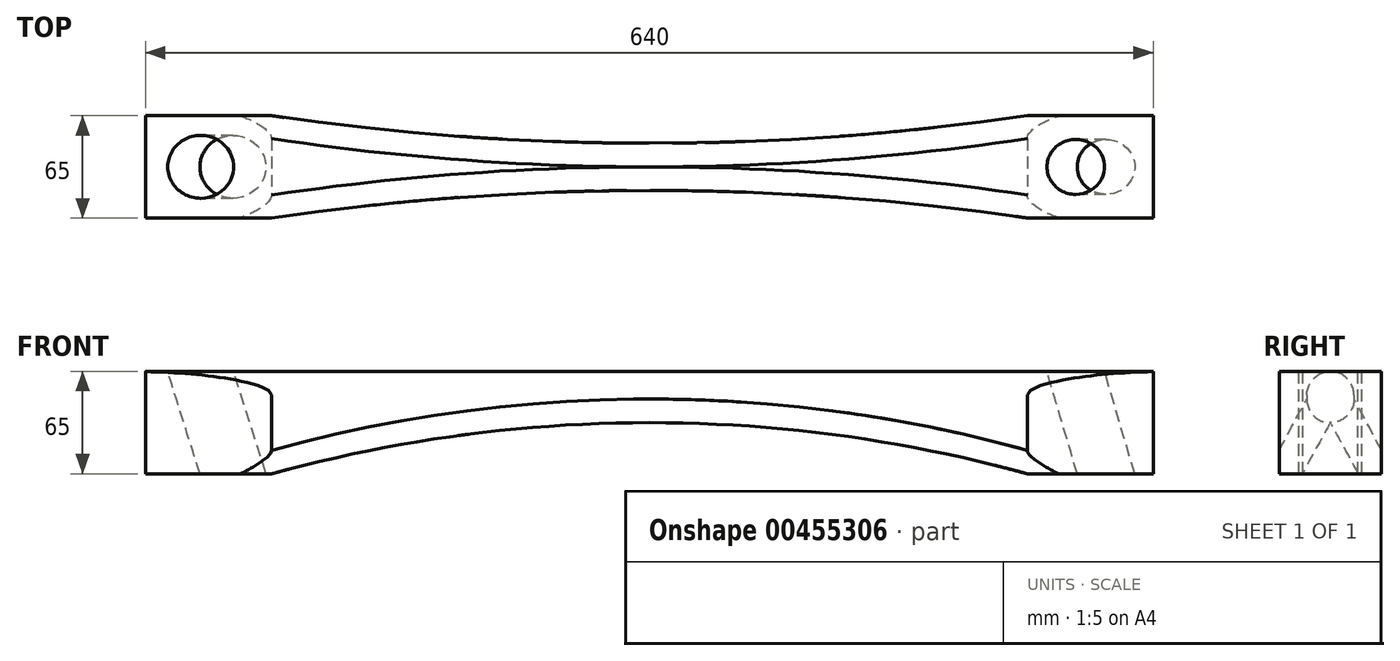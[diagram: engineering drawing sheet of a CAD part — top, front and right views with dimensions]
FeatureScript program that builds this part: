
annotation { "Feature Type Name" : "Feature", "Feature Type Description" : "" }
export const myFeature = defineFeature(function(context is Context, id is Id, definition is map)
    precondition{}
    {
        {
            var Q0;
            Q0=qCreatedBy(makeId("Front.planeOp"),FACE);
            var sketch = newSketch(context, id + "F0", { "sketchPlane" : qUnion([Q0])});
            skLineSegment(sketch, "E0.bottom", {"start": v(0, 0) * mm, "end": v(-640, 0) * mm});
            skLineSegment(sketch, "E0.top", {"start": v(0, 65) * mm, "end": v(-640, 65) * mm});
            skLineSegment(sketch, "E0.left", {"start": v(0, 0) * mm, "end": v(0, 65) * mm});
            skLineSegment(sketch, "E0.right", {"start": v(-640, 0) * mm, "end": v(-640, 65) * mm});
            skSolve(sketch);
        }
        {
            var Q0;
            Q0 = qSketchRegion(id + "F0", true);
            extrude(context, id + "F1", {"entities" : qUnion([Q0]), "depth" : 65 * mm, "offsetDistance" : 25 * mm});
        }
        {
            var Q0;
            Q0=makeQuery(id+"F1.opExtrude","SWEPT_FACE",FACE,{"disambiguationData":[OSD([sQuery(id+"F0.wireOp",EDGE,"E0.bottom")])]});
            var sketch = newSketch(context, id + "F2", { "sketchPlane" : qUnion([Q0])});
            skLineSegment(sketch, "E1", {"start": v(-30, 65) * mm, "end": v(-30, 0) * mm, "construction": true});
            skLineSegment(sketch, "E2", {"start": v(-601, 65) * mm, "end": v(-601, 0) * mm, "construction": true});
            skSolve(sketch);
        }
        {
            var Q0;
            Q0=sQuery(id+"F2.wireOp",EDGE,"E1");
            cPlane(context, id + "F3", {"entities" : qUnion([Q0]), "cplaneType" : CPlaneType.LINE_ANGLE, "offset" : 25 * mm, "angle" : 16.5 * degree, "oppositeDirection" : true, "width" : 150 * mm, "height" : 150 * mm});
        }
        {
            var Q0;
            Q0=qCreatedBy(id+"F3.planeOp",FACE);
            var sketch = newSketch(context, id + "F4", { "sketchPlane" : qUnion([Q0])});
            skLineSegment(sketch, "E3.0", {"start": v(0, -65) * mm, "end": v(0, 0) * mm, "construction": true});
            skLineSegment(sketch, "E4", {"start": v(0, -32.5) * mm, "end": v(-90.45, -32.5) * mm, "construction": true});
            skLineSegment(sketch, "E5.0", {"start": v(-28.76, -65) * mm, "end": v(-28.76, 0) * mm, "construction": true});
            skCircle(sketch, "E6", {"center": v(-28.76, -32.5) * mm, "radius": 17.5 * mm});
            skSolve(sketch);
        }
        {
            var Q0;
            Q0 = qSketchRegion(id + "F4", true);
            extrude(context, id + "F5", {"entities" : qUnion([Q0]), "operationType" : NewBodyOperationType.REMOVE, "oppositeDirection" : true, "depth" : 8 * mm, "offsetDistance" : 25 * mm, "hasSecondDirection" : true, "secondDirectionOppositeDirection" : false, "secondDirectionDepth" : 87 * mm});
        }
        {
            var Q0;
            Q0=makeQuery(id+"F1.opExtrude","SWEPT_FACE",FACE,{"disambiguationData":[OSD([sQuery(id+"F0.wireOp",EDGE,"E0.top")])]});
            var sketch = newSketch(context, id + "F6", { "sketchPlane" : qUnion([Q0])});
            skLineSegment(sketch, "E7", {"start": v(-605, 0) * mm, "end": v(-605, -65) * mm, "construction": true});
            skSolve(sketch);
        }
        {
            var Q0;
            Q0=sQuery(id+"F6.wireOp",EDGE,"E7");
            cPlane(context, id + "F7", {"entities" : qUnion([Q0]), "cplaneType" : CPlaneType.LINE_ANGLE, "offset" : 25 * mm, "angle" : 17.5 * degree, "width" : 150 * mm, "height" : 150 * mm});
        }
        {
            var Q0;
            Q0=qCreatedBy(id+"F7.planeOp",FACE);
            var sketch = newSketch(context, id + "F8", { "sketchPlane" : qUnion([Q0])});
            skLineSegment(sketch, "E8.0", {"start": v(-590.83, 65) * mm, "end": v(-590.83, 0) * mm, "construction": true});
            skLineSegment(sketch, "E9", {"start": v(-590.83, 32.5) * mm, "end": v(-455.25, 32.5) * mm, "construction": true});
            skLineSegment(sketch, "E10.0", {"start": v(-557.45, 0) * mm, "end": v(-557.45, 65) * mm, "construction": true});
            skCircle(sketch, "E11", {"center": v(-557.45, 32.5) * mm, "radius": 20 * mm});
            skSolve(sketch);
        }
        {
            var Q0;
            Q0 = qSketchRegion(id + "F8", true);
            extrude(context, id + "F9", {"entities" : qUnion([Q0]), "operationType" : NewBodyOperationType.REMOVE, "depth" : 92 * mm, "offsetDistance" : 25 * mm, "hasSecondDirection" : true, "secondDirectionOppositeDirection" : true, "secondDirectionDepth" : 83 * mm});
        }
        {
            var Q0;
            Q0=makeQuery(id+"F1.opExtrude","CAP_FACE",FACE,{"disambiguationData":[OSD([sQuery(id+"F0.wireOp",EDGE,"E0.bottom"),sQuery(id+"F0.wireOp",EDGE,"E0.top"),sQuery(id+"F0.wireOp",EDGE,"E0.left"),sQuery(id+"F0.wireOp",EDGE,"E0.right")])],"isStart":false});
            var sketch = newSketch(context, id + "F10", { "sketchPlane" : qUnion([Q0])});
            skLineSegment(sketch, "E12.0", {"start": v(-640, 0) * mm, "end": v(-640, 65) * mm, "construction": true});
            skLineSegment(sketch, "E13.0", {"start": v(0, 0) * mm, "end": v(0, 65) * mm, "construction": true});
            skLineSegment(sketch, "E14", {"start": v(0, 32.5) * mm, "end": v(-640, 32.5) * mm, "construction": true});
            skLineSegment(sketch, "E15.0", {"start": v(0, 47.5) * mm, "end": v(-640, 47.5) * mm, "construction": true});
            skLineSegment(sketch, "E16.0", {"start": v(0, 17.5) * mm, "end": v(-640, 17.5) * mm, "construction": true});
            skLineSegment(sketch, "E17", {"start": v(-80, 0) * mm, "end": v(-80, 65) * mm, "construction": true});
            skLineSegment(sketch, "E18", {"start": v(-320, 47.5) * mm, "end": v(-320, 17.5) * mm, "construction": true});
            skLineSegment(sketch, "E19.MirrorCS", {"start": v(-560, 0) * mm, "end": v(-560, 65) * mm, "construction": true});
            skLineSegment(sketch, "E20", {"start": v(-560, 0) * mm, "end": v(-80, 0) * mm});
            skArc(sketch, "E21.MirrorCS", {"start": v(-560, 0) * mm, "mid": v(-320, 32.5) * mm, "end": v(-80, 0) * mm});
            skSolve(sketch);
        }
        {
            var Q0;
            Q0 = qSketchRegion(id + "F10", true);
            extrude(context, id + "F11", {"entities" : qUnion([Q0]), "operationType" : NewBodyOperationType.REMOVE, "endBound" : BoundingType.THROUGH_ALL, "oppositeDirection" : true, "depth" : 25 * mm, "offsetDistance" : 25 * mm});
        }
        {
            var Q0;
            {var subQ0=sQuery(id+"F0.wireOp",EDGE,"E0.bottom");Q0=makeQuery(id+"F2.imprint","IMPRINT",FACE,{"disambiguationData":[TD([[makeQuery(id+"F2.imprint","IMPRINT",EDGE,{"derivedFrom":makeQuery(id+"F1.opExtrude","CAP_EDGE",EDGE,{"disambiguationData":[OSD([subQ0])],"isStart":true})}),-1.0]])]});}
            var sketch = newSketch(context, id + "F12", { "sketchPlane" : qUnion([Q0])});
            skLineSegment(sketch, "E22.0", {"start": v(-640, 65) * mm, "end": v(-640, 0) * mm, "construction": true});
            skLineSegment(sketch, "E23.0", {"start": v(0, 65) * mm, "end": v(0, 0) * mm, "construction": true});
            skLineSegment(sketch, "E24", {"start": v(0, 32.5) * mm, "end": v(-640, 32.5) * mm, "construction": true});
            skLineSegment(sketch, "E25.0", {"start": v(0, 47.5) * mm, "end": v(-650, 47.5) * mm, "construction": true});
            skLineSegment(sketch, "E26.0", {"start": v(0, 17.5) * mm, "end": v(-650, 17.5) * mm, "construction": true});
            skLineSegment(sketch, "E27.0", {"start": v(-80, 65) * mm, "end": v(-80, 0) * mm, "construction": true});
            skLineSegment(sketch, "E28.0", {"start": v(-560, 65) * mm, "end": v(-560, 0) * mm, "construction": true});
            skArc(sketch, "E29", {"start": v(-80, 0) * mm, "mid": v(-320, 17.5) * mm, "end": v(-560, 0) * mm});
            skArc(sketch, "E30", {"start": v(-560, 65) * mm, "mid": v(-320, 47.5) * mm, "end": v(-80, 65) * mm});
            skLineSegment(sketch, "E31", {"start": v(-80, 0) * mm, "end": v(-560, 0) * mm});
            skLineSegment(sketch, "E32", {"start": v(-80, 65) * mm, "end": v(-560, 65) * mm});
            skSolve(sketch);
        }
        {
            var Q0;
            Q0 = qSketchRegion(id + "F12", true);
            extrude(context, id + "F13", {"entities" : qUnion([Q0]), "operationType" : NewBodyOperationType.REMOVE, "endBound" : BoundingType.THROUGH_ALL, "oppositeDirection" : true, "depth" : 25 * mm, "offsetDistance" : 25 * mm});
        }
        {
            var Q0;
            Q0=makeQuery(id+"F13.boolean.opBoolean","INTERSECT",EDGE,{"derivedFrom":[makeQuery(id+"F1.opExtrude","SWEPT_FACE",FACE,{"disambiguationData":[OSD([sQuery(id+"F0.wireOp",EDGE,"E0.top")])]}),makeQuery(id+"F13.opExtrude","SWEPT_FACE",FACE,{"disambiguationData":[OSD([sQuery(id+"F12.wireOp",EDGE,"E30")])]})]});
            var Q1;
            Q1=makeQuery(id+"F13.boolean.opBoolean","INTERSECT",EDGE,{"derivedFrom":[makeQuery(id+"F1.opExtrude","SWEPT_FACE",FACE,{"disambiguationData":[OSD([sQuery(id+"F0.wireOp",EDGE,"E0.top")])]}),makeQuery(id+"F13.opExtrude","SWEPT_FACE",FACE,{"disambiguationData":[OSD([sQuery(id+"F12.wireOp",EDGE,"E29")])]})]});
            var Q2;
            Q2=makeQuery(id+"F13.boolean.opBoolean","INTERSECT",EDGE,{"derivedFrom":[makeQuery(id+"F11.boolean.opBoolean","COPY",FACE,{"derivedFrom":makeQuery(id+"F11.opExtrude","SWEPT_FACE",FACE,{"disambiguationData":[OSD([sQuery(id+"F10.wireOp",EDGE,"E21.MirrorCS")])]})}),makeQuery(id+"F13.opExtrude","SWEPT_FACE",FACE,{"disambiguationData":[OSD([sQuery(id+"F12.wireOp",EDGE,"E30")])]})]});
            var Q3;
            Q3=makeQuery(id+"F13.boolean.opBoolean","INTERSECT",EDGE,{"derivedFrom":[makeQuery(id+"F11.boolean.opBoolean","COPY",FACE,{"derivedFrom":makeQuery(id+"F11.opExtrude","SWEPT_FACE",FACE,{"disambiguationData":[OSD([sQuery(id+"F10.wireOp",EDGE,"E21.MirrorCS")])]})}),makeQuery(id+"F13.opExtrude","SWEPT_FACE",FACE,{"disambiguationData":[OSD([sQuery(id+"F12.wireOp",EDGE,"E29")])]})]});
            fillet(context, id + "F14", {"entities" : qUnion([Q0, Q1, Q2, Q3]), "radius" : 15 * mm, "tangentPropagation" : true, "allowEdgeOverflow" : false});
        }
    });
